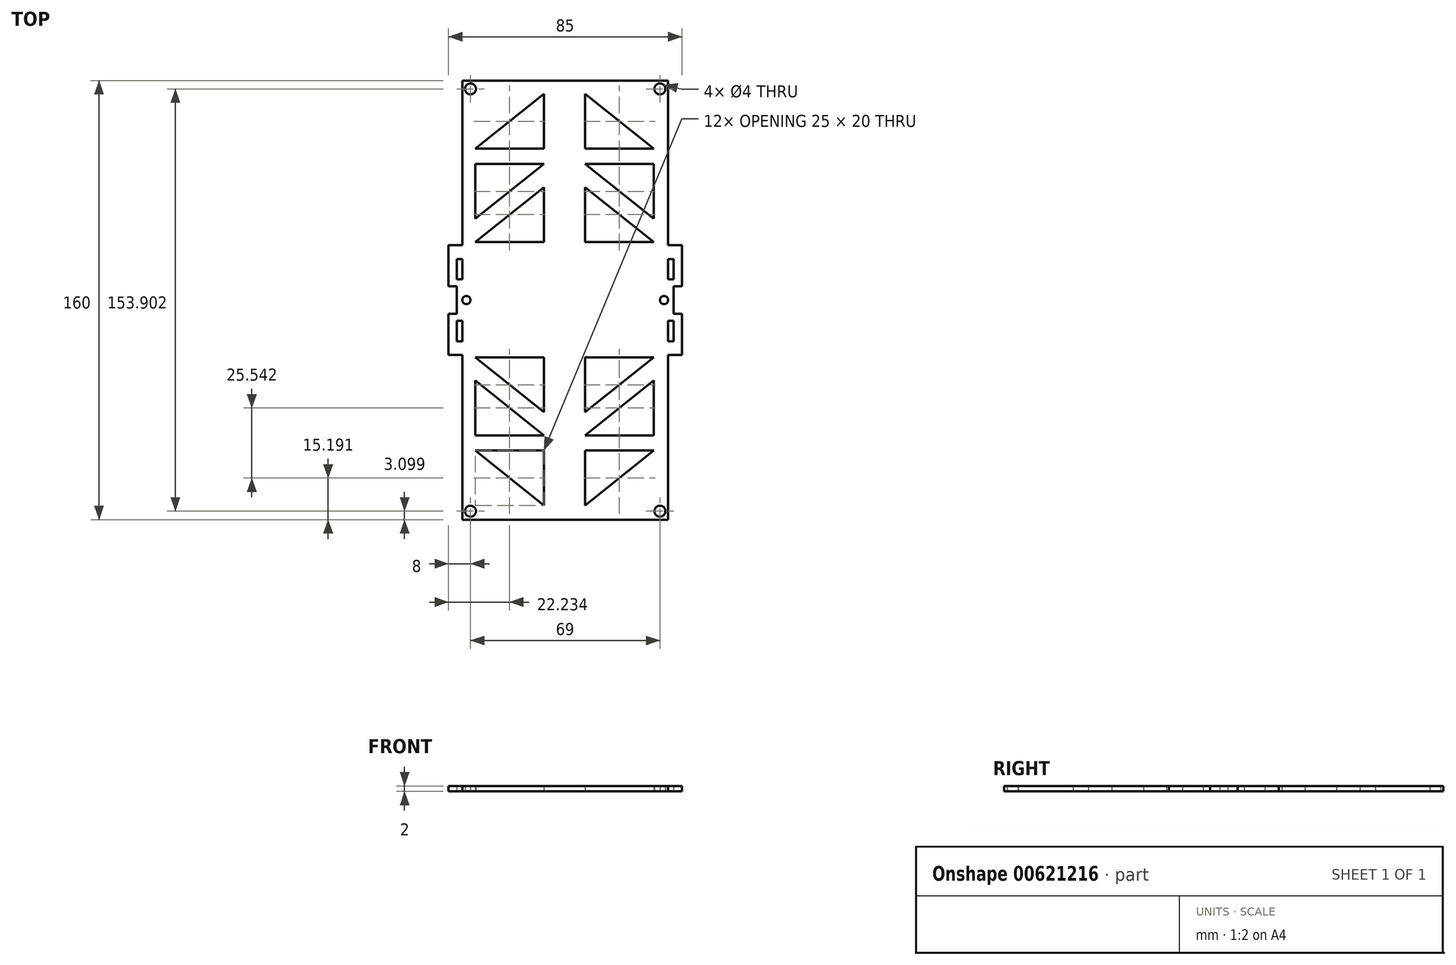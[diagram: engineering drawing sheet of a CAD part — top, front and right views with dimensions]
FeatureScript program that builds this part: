
annotation { "Feature Type Name" : "Feature", "Feature Type Description" : "" }
export const myFeature = defineFeature(function(context is Context, id is Id, definition is map)
    precondition{}
    {
        {
            var Q0;
            Q0=qCreatedBy(makeId("Top.planeOp"),FACE);
            var sketch = newSketch(context, id + "F0", { "sketchPlane" : qUnion([Q0])});
            skLineSegment(sketch, "E0.bottom", {"start": v(-37.5, 79.95) * mm, "end": v(37.5, 79.95) * mm});
            skLineSegment(sketch, "E0.top", {"start": v(-37.5, -80.05) * mm, "end": v(37.5, -80.05) * mm});
            skLineSegment(sketch, "E0.left", {"start": v(-37.5, 79.95) * mm, "end": v(-37.5, -80.05) * mm});
            skLineSegment(sketch, "E0.right", {"start": v(37.5, 79.95) * mm, "end": v(37.5, -80.05) * mm});
            skPoint(sketch, "E0.middle", {"position": v(0, -0.05) * mm});
            skLineSegment(sketch, "E1.bottom", {"start": v(-37.5, -20) * mm, "end": v(-39.5, -20) * mm});
            skLineSegment(sketch, "E1.top", {"start": v(-37.5, 20) * mm, "end": v(-39.5, 20) * mm});
            skLineSegment(sketch, "E1.left", {"start": v(-37.5, -20) * mm, "end": v(-37.5, 20) * mm});
            skLineSegment(sketch, "E1.right", {"start": v(-39.5, -20) * mm, "end": v(-39.5, 20) * mm});
            skLineSegment(sketch, "E2.MirrorCS", {"start": v(39.5, -15.06) * mm, "end": v(39.5, 14.94) * mm});
            skLineSegment(sketch, "E3.MirrorCS", {"start": v(37.5, -15.06) * mm, "end": v(39.5, -15.06) * mm});
            skLineSegment(sketch, "E4.MirrorCS", {"start": v(37.5, 14.94) * mm, "end": v(39.5, 14.94) * mm});
            skLineSegment(sketch, "E5", {"start": v(-32.77, 55.14) * mm, "end": v(-7.77, 75.14) * mm});
            skLineSegment(sketch, "E6", {"start": v(-7.77, 55.14) * mm, "end": v(-7.77, 75.14) * mm});
            skLineSegment(sketch, "E7", {"start": v(-7.77, 55.14) * mm, "end": v(-32.77, 55.14) * mm});
            skLineSegment(sketch, "E8.MirrorCS", {"start": v(7.23, 55.14) * mm, "end": v(32.23, 55.14) * mm});
            skLineSegment(sketch, "E9.MirrorCS", {"start": v(32.23, 55.14) * mm, "end": v(7.23, 75.14) * mm});
            skLineSegment(sketch, "E10.MirrorCS", {"start": v(7.23, 55.14) * mm, "end": v(7.23, 75.14) * mm});
            skLineSegment(sketch, "E11.MirrorCS", {"start": v(-7.77, -54.86) * mm, "end": v(-32.77, -54.86) * mm});
            skLineSegment(sketch, "E12.MirrorCS", {"start": v(-32.77, -54.86) * mm, "end": v(-7.77, -74.86) * mm});
            skLineSegment(sketch, "E13.MirrorCS", {"start": v(-7.77, -54.86) * mm, "end": v(-7.77, -74.86) * mm});
            skLineSegment(sketch, "E14.MirrorCS", {"start": v(7.23, -54.86) * mm, "end": v(7.23, -74.86) * mm});
            skLineSegment(sketch, "E15.MirrorCS", {"start": v(7.23, -54.86) * mm, "end": v(32.23, -54.86) * mm});
            skLineSegment(sketch, "E16.MirrorCS", {"start": v(32.23, -54.86) * mm, "end": v(7.23, -74.86) * mm});
            skLineSegment(sketch, "E17.MirrorCS", {"start": v(-7.77, 21.14) * mm, "end": v(-32.77, 21.14) * mm});
            skLineSegment(sketch, "E18.MirrorCS", {"start": v(-32.77, 21.14) * mm, "end": v(-7.77, 41.14) * mm});
            skLineSegment(sketch, "E19.MirrorCS", {"start": v(-7.77, 21.14) * mm, "end": v(-7.77, 41.14) * mm});
            skLineSegment(sketch, "E20.MirrorCS", {"start": v(7.23, 21.14) * mm, "end": v(7.23, 41.14) * mm});
            skLineSegment(sketch, "E21.MirrorCS", {"start": v(32.23, 21.14) * mm, "end": v(7.23, 41.14) * mm});
            skLineSegment(sketch, "E22.MirrorCS", {"start": v(7.23, 21.14) * mm, "end": v(32.23, 21.14) * mm});
            skLineSegment(sketch, "E23.MirrorCS", {"start": v(-7.77, -20.86) * mm, "end": v(-32.77, -20.86) * mm});
            skLineSegment(sketch, "E24.MirrorCS", {"start": v(-32.77, -20.86) * mm, "end": v(-7.77, -40.86) * mm});
            skLineSegment(sketch, "E25.MirrorCS", {"start": v(7.23, -20.86) * mm, "end": v(7.23, -40.86) * mm});
            skLineSegment(sketch, "E26.MirrorCS", {"start": v(32.23, -20.86) * mm, "end": v(7.23, -40.86) * mm});
            skLineSegment(sketch, "E27.MirrorCS", {"start": v(7.23, -20.86) * mm, "end": v(32.23, -20.86) * mm});
            skLineSegment(sketch, "E28.MirrorCS", {"start": v(-7.77, -20.86) * mm, "end": v(-7.77, -40.86) * mm});
            skLineSegment(sketch, "E29", {"start": v(-32.77, 29.6) * mm, "end": v(-7.77, 49.6) * mm});
            skLineSegment(sketch, "E30", {"start": v(-7.77, 49.6) * mm, "end": v(-32.77, 49.6) * mm});
            skLineSegment(sketch, "E31", {"start": v(-32.77, 49.6) * mm, "end": v(-32.77, 29.6) * mm});
            skLineSegment(sketch, "E32.MirrorCS", {"start": v(32.23, 29.6) * mm, "end": v(7.23, 49.6) * mm});
            skLineSegment(sketch, "E33.MirrorCS", {"start": v(7.23, 49.6) * mm, "end": v(32.23, 49.6) * mm});
            skLineSegment(sketch, "E34.MirrorCS", {"start": v(32.23, 49.6) * mm, "end": v(32.23, 29.6) * mm});
            skLineSegment(sketch, "E35.MirrorCS", {"start": v(-32.77, -29.32) * mm, "end": v(-7.77, -49.32) * mm});
            skLineSegment(sketch, "E36.MirrorCS", {"start": v(-32.77, -49.32) * mm, "end": v(-32.77, -29.32) * mm});
            skLineSegment(sketch, "E37.MirrorCS", {"start": v(-7.77, -49.32) * mm, "end": v(-32.77, -49.32) * mm});
            skLineSegment(sketch, "E38.MirrorCS", {"start": v(7.23, -49.32) * mm, "end": v(32.23, -49.32) * mm});
            skLineSegment(sketch, "E39.MirrorCS", {"start": v(32.23, -29.32) * mm, "end": v(7.23, -49.32) * mm});
            skLineSegment(sketch, "E40.MirrorCS", {"start": v(32.23, -49.32) * mm, "end": v(32.23, -29.32) * mm});
            skLineSegment(sketch, "E41.MirrorCS", {"start": v(39.5, -20) * mm, "end": v(39.5, 20) * mm});
            skLineSegment(sketch, "E42.MirrorCS", {"start": v(37.5, 20) * mm, "end": v(39.5, 20) * mm});
            skLineSegment(sketch, "E43.MirrorCS", {"start": v(37.5, -20) * mm, "end": v(39.5, -20) * mm});
            skLineSegment(sketch, "E44.MirrorCS", {"start": v(-37.5, -15.06) * mm, "end": v(-39.5, -15.06) * mm});
            skLineSegment(sketch, "E45.MirrorCS", {"start": v(-37.5, 14.94) * mm, "end": v(-39.5, 14.94) * mm});
            skLineSegment(sketch, "E46.bottom", {"start": v(-37.5, 7.5) * mm, "end": v(-39.5, 7.5) * mm});
            skLineSegment(sketch, "E46.top", {"start": v(-37.5, -7.5) * mm, "end": v(-39.5, -7.5) * mm});
            skLineSegment(sketch, "E46.left", {"start": v(-37.5, 7.5) * mm, "end": v(-37.5, -7.5) * mm});
            skLineSegment(sketch, "E46.right", {"start": v(-39.5, 7.5) * mm, "end": v(-39.5, -7.5) * mm});
            skLineSegment(sketch, "E47.MirrorCS", {"start": v(37.5, 7.5) * mm, "end": v(39.5, 7.5) * mm});
            skLineSegment(sketch, "E48.MirrorCS", {"start": v(37.5, -7.5) * mm, "end": v(39.5, -7.5) * mm});
            skLineSegment(sketch, "E49.bottom", {"start": v(-39.5, 20) * mm, "end": v(-42.5, 20) * mm});
            skLineSegment(sketch, "E49.top", {"start": v(-39.5, -20) * mm, "end": v(-42.5, -20) * mm});
            skLineSegment(sketch, "E49.left", {"start": v(-39.5, 20) * mm, "end": v(-39.5, -20) * mm});
            skLineSegment(sketch, "E49.right", {"start": v(-42.5, 20) * mm, "end": v(-42.5, -20) * mm});
            skLineSegment(sketch, "E50.MirrorCS", {"start": v(-45.5, 20) * mm, "end": v(-42.5, 20) * mm});
            skLineSegment(sketch, "E51.MirrorCS", {"start": v(42.5, 20) * mm, "end": v(42.5, -20) * mm});
            skLineSegment(sketch, "E52.MirrorCS", {"start": v(39.5, 20) * mm, "end": v(42.5, 20) * mm});
            skLineSegment(sketch, "E53.MirrorCS", {"start": v(39.5, -20) * mm, "end": v(42.5, -20) * mm});
            skCircle(sketch, "E54", {"center": v(-34.5, 76.95) * mm, "radius": 2 * mm});
            skCircle(sketch, "E55.MirrorC", {"center": v(34.5, 76.95) * mm, "radius": 2 * mm});
            skCircle(sketch, "E56.MirrorC", {"center": v(-34.5, -76.95) * mm, "radius": 2 * mm});
            skCircle(sketch, "E57.MirrorC", {"center": v(34.5, -76.95) * mm, "radius": 2 * mm});
            skLineSegment(sketch, "E58.bottom", {"start": v(-39.5, 5) * mm, "end": v(-42.5, 5) * mm});
            skLineSegment(sketch, "E58.top", {"start": v(-39.5, -5) * mm, "end": v(-42.5, -5) * mm});
            skLineSegment(sketch, "E58.left", {"start": v(-39.5, 5) * mm, "end": v(-39.5, -5) * mm});
            skLineSegment(sketch, "E58.right", {"start": v(-42.5, 5) * mm, "end": v(-42.5, -5) * mm});
            skLineSegment(sketch, "E59.MirrorCS", {"start": v(39.5, 5) * mm, "end": v(42.5, 5) * mm});
            skLineSegment(sketch, "E60.MirrorCS", {"start": v(39.5, -5) * mm, "end": v(42.5, -5) * mm});
            skCircle(sketch, "E61", {"center": v(-36, 0) * mm, "radius": 1.5 * mm});
            skCircle(sketch, "E62.MirrorC", {"center": v(36, 0) * mm, "radius": 1.5 * mm});
            skSolve(sketch);
        }
        {
            var Q0;
            {var subQ3=sQuery(id+"F0.wireOp",EDGE,"E0.bottom");Q0=makeQuery(id+"F0.imprint","IMPRINT",FACE,{"disambiguationData":[TD([[makeQuery(id+"F0.imprint","IMPRINT",EDGE,{"derivedFrom":subQ3}),-1.0]])]});}
            var Q1;
            Q1=makeQuery(id+"F0.imprint","IMPRINT",FACE,{"disambiguationData":[TD([[makeQuery(id+"F0.imprint","IMPRINT",EDGE,{"derivedFrom":sQuery(id+"F0.wireOp",EDGE,"E2.MirrorCS")}),1.0]])]});
            var Q2;
            Q2=makeQuery(id+"F0.imprint","IMPRINT",FACE,{"disambiguationData":[TD([[makeQuery(id+"F0.imprint","IMPRINT",EDGE,{"derivedFrom":sQuery(id+"F0.wireOp",EDGE,"E46.bottom")}),1.0]])]});
            var Q3;
            {var subQ0=sQuery(id+"F0.wireOp",EDGE,"E4.MirrorCS");var subQ1=sQuery(id+"F0.wireOp",EDGE,"E0.right");var subQ2=makeQuery(id+"F0.imprint","INTERSECT",VERTEX,{"derivedFrom":[subQ1,subQ0]});Q3=makeQuery(id+"F0.imprint","IMPRINT",FACE,{"disambiguationData":[TD([[makeQuery(id+"F0.imprint","IMPRINT",EDGE,{"disambiguationData":[TD([[subQ2,1.0]])],"derivedFrom":subQ1}),1.0]])]});}
            var Q4;
            {var subQ0=sQuery(id+"F0.wireOp",EDGE,"E47.MirrorCS");var subQ1=sQuery(id+"F0.wireOp",EDGE,"E0.right");var subQ2=makeQuery(id+"F0.imprint","INTERSECT",VERTEX,{"derivedFrom":[subQ1,subQ0]});Q4=makeQuery(id+"F0.imprint","IMPRINT",FACE,{"disambiguationData":[TD([[makeQuery(id+"F0.imprint","IMPRINT",EDGE,{"disambiguationData":[TD([[subQ2,-1.0]])],"derivedFrom":subQ1}),1.0]])]});}
            var Q5;
            {var subQ0=sQuery(id+"F0.wireOp",EDGE,"E3.MirrorCS");var subQ1=sQuery(id+"F0.wireOp",EDGE,"E0.right");var subQ2=makeQuery(id+"F0.imprint","INTERSECT",VERTEX,{"derivedFrom":[subQ1,subQ0]});Q5=makeQuery(id+"F0.imprint","IMPRINT",FACE,{"disambiguationData":[TD([[makeQuery(id+"F0.imprint","IMPRINT",EDGE,{"disambiguationData":[TD([[subQ2,-1.0]])],"derivedFrom":subQ1}),1.0]])]});}
            var Q6;
            {var subQ0=sQuery(id+"F0.wireOp",EDGE,"E1.bottom");Q6=makeQuery(id+"F0.imprint","IMPRINT",FACE,{"disambiguationData":[TD([[makeQuery(id+"F0.imprint","IMPRINT",EDGE,{"derivedFrom":subQ0}),-1.0]])]});}
            var Q7;
            {var subQ0=sQuery(id+"F0.wireOp",EDGE,"E1.top");Q7=makeQuery(id+"F0.imprint","IMPRINT",FACE,{"disambiguationData":[TD([[makeQuery(id+"F0.imprint","IMPRINT",EDGE,{"derivedFrom":subQ0}),1.0]])]});}
            var Q8;
            {var subQ3=sQuery(id+"F0.wireOp",EDGE,"E49.bottom");Q8=makeQuery(id+"F0.imprint","IMPRINT",FACE,{"disambiguationData":[TD([[makeQuery(id+"F0.imprint","IMPRINT",EDGE,{"derivedFrom":subQ3}),1.0]])]});}
            var Q9;
            {var subQ0=sQuery(id+"F0.wireOp",EDGE,"E52.MirrorCS");Q9=makeQuery(id+"F0.imprint","IMPRINT",FACE,{"disambiguationData":[TD([[makeQuery(id+"F0.imprint","IMPRINT",EDGE,{"derivedFrom":subQ0}),-1.0]])]});}
            var Q10;
            {var subQ0=sQuery(id+"F0.wireOp",EDGE,"E53.MirrorCS");Q10=makeQuery(id+"F0.imprint","IMPRINT",FACE,{"disambiguationData":[TD([[makeQuery(id+"F0.imprint","IMPRINT",EDGE,{"derivedFrom":subQ0}),1.0]])]});}
            var Q11;
            {var subQ1=sQuery(id+"F0.wireOp",EDGE,"E49.top");Q11=makeQuery(id+"F0.imprint","IMPRINT",FACE,{"disambiguationData":[TD([[makeQuery(id+"F0.imprint","IMPRINT",EDGE,{"derivedFrom":subQ1}),-1.0]])]});}
            extrude(context, id + "F1", {"entities" : qUnion([Q0, Q1, Q2, Q3, Q4, Q5, Q6, Q7, Q8, Q9, Q10, Q11]), "depth" : 2 * mm, "offsetDistance" : 25 * mm});
        }
    });
